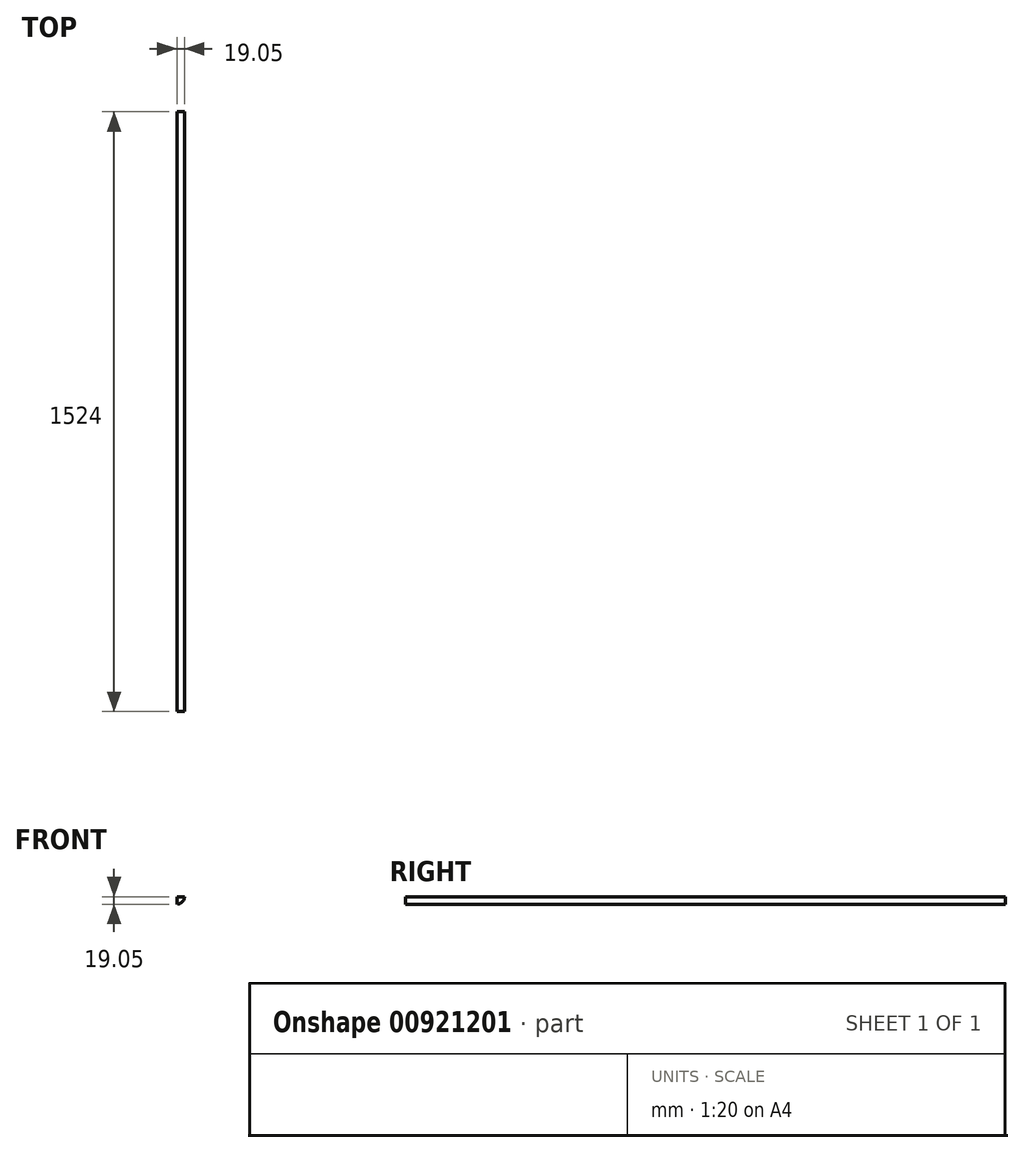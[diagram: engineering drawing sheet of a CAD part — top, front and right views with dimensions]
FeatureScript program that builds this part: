
annotation { "Feature Type Name" : "Feature", "Feature Type Description" : "" }
export const myFeature = defineFeature(function(context is Context, id is Id, definition is map)
    precondition{}
    {
        {
            var Q0;
            Q0=qCreatedBy(makeId("Front.planeOp"),FACE);
            var sketch = newSketch(context, id + "F0", { "sketchPlane" : qUnion([Q0])});
            skLineSegment(sketch, "E0", {"start": v(0, 0) * mm, "end": v(19.05, 0) * mm});
            skLineSegment(sketch, "E1", {"start": v(0, 0) * mm, "end": v(0, -19.05) * mm});
            skArc(sketch, "E2", {"start": v(0, -19.05) * mm, "mid": v(13.47, -13.47) * mm, "end": v(19.05, 0) * mm});
            skSolve(sketch);
        }
        {
            var Q0;
            Q0=makeQuery(id+"F0.imprint","IMPRINT",FACE,{"disambiguationData":[TD([[makeQuery(id+"F0.imprint","IMPRINT",EDGE,{"derivedFrom":sQuery(id+"F0.wireOp",EDGE,"E0")}),-1.0]])]});
            extrude(context, id + "F1", {"entities" : qUnion([Q0]), "depth" : 1524 * mm, "offsetDistance" : 25.4 * mm});
        }
    });
